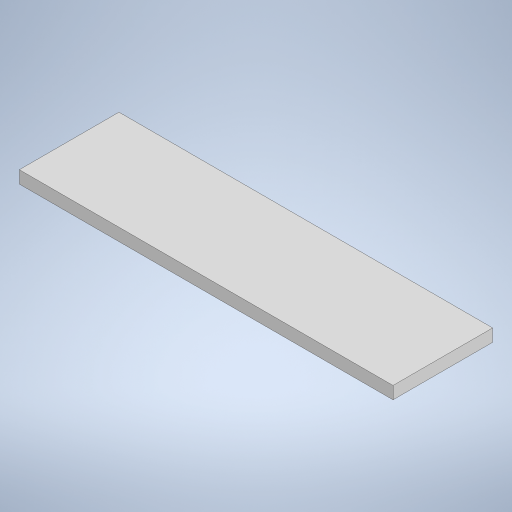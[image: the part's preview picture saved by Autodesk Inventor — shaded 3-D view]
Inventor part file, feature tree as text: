
AUTODESK INVENTOR PART (.ipt)
format: ipt  version: 2024.2 (Build 282272000, 272)  size: 210,432 bytes
history: native  units: mm
features: other x1, extrude x1, sketch x1
ambient origin geometry x8: Origin, YZ Plane, XZ Plane, XY Plane, X Axis, Y Axis, Z Axis, Center Point
bodies: Body1 (feature_tree)
feature tree (3):
  other  "Bryła1"
  extrude  "Wyciągnięcie proste1"  Depth=8.0mm
  sketch  "Szkic1"
